# Revit family: Турникет трипод PERCo_TTR-08А
name_source: partatom
category: Mechanical Equipment
units: mm (PartAtom-declared; Revit-internal decimal feet)

## family parameters
Always vertical = Yes
Classification = None
Cut with Voids When Loaded = No
Part Type = Normal
Room Calculation Point = No
Round Connector Dimension = Use Diameter
Shared = No
Work Plane-Based = No

## types (1)
- TTR-08А
    Built-in reader = Yes
    Colour = Stainless steel
    Cost = 0 $
    Current = 6 A
    Dimensions = 777×798×1084 mm
    Electrical connection = 220 B
    Full name = TTR-08A Electromechanical Tripod Turnstile with Automatic Anti-Panic Barrier Arms
    IP Code = IP54
    Manufacturer = PERCo
    Material = Housing ─ high-quality stainless steel with ABS plastic inserts. Barrier arms ─ stainless steel.
    Maximum dimensions of ACS controller = max. 240×200×35 mm
    Maximum dimensions of installed readers = max. 145×90×25 mm
    Name = TTR-08А Tripod Turnstile
    Number = 1
    Operating temperature = from -20°С to +50°С
    Passageway width = 500 mm
    Plank length = 538 mm  [stored 1.76509 ft]
    Plank voltage = 72
    Throughput rate = 30 persons/min
    Type Image = <None>
    URL = https://www.perco.com
    Unit of measurement = pcs
    Voltage = 12 V
    Weight = max. 37 kg
    Материал планок = Stainless_steel
    Окраска турникета = Stainless steel
    Основание планок = Black

note: source unit labels omitted for Plank voltage — the stored unit's dimension contradicts the parameter name (converter mislabeling)

note: [stored X ft] marks values corroborated as IEEE doubles in the binary element streams (Revit-internal decimal feet)
